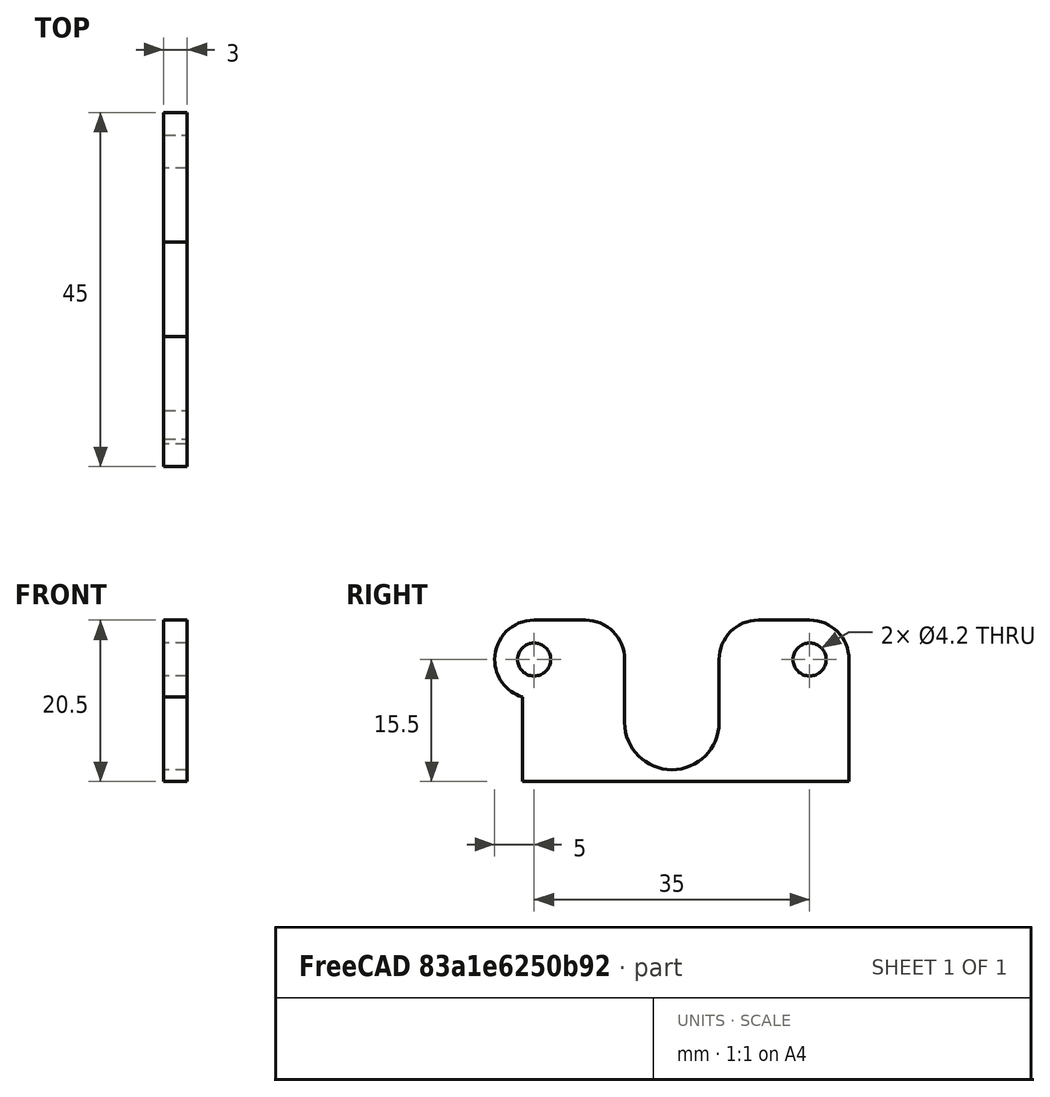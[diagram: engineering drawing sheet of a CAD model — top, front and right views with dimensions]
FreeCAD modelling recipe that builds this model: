
FCSTD DOCUMENT  (FreeCAD 0.16R6712 (Git))
Label: stepperMount_v01
License: All rights reserved
LicenseURL: http://en.wikipedia.org/wiki/All_rights_reserved
objects: Sketcher::SketchObject×1, PartDesign::Pad×1
note: 3 computed .brp shape members not serialized (recipe doc carries the construction recipe); baked Part::Feature solids carry a one-line shape summary decoded from their .brp

FEATURE [Sketcher::SketchObject] Sketch  label="StepperMount"
  Placement = pos=(0,0,0) rot=(0.57735,0.57735,0.57735;2.0944rad)
  sketch-geometry (15):
    g0: Circle CenterX=-17.5 CenterY=14 CenterZ=0 NormalX=0 NormalY=0 NormalZ=1 Radius=2.1
    g1: Circle CenterX=17.5 CenterY=14 CenterZ=0 NormalX=0 NormalY=0 NormalZ=1 Radius=2.1
    g2: ArcOfCircle CenterX=-17.5 CenterY=14 CenterZ=0 NormalX=0 NormalY=0 NormalZ=1 Radius=5 StartAngle=1.5708 EndAngle=3.14159
    g3: ArcOfCircle CenterX=17.5 CenterY=14 CenterZ=0 NormalX=0 NormalY=0 NormalZ=1 Radius=5 StartAngle=0 EndAngle=1.5708
    g4: ArcOfCircle CenterX=0 CenterY=6 CenterZ=0 NormalX=0 NormalY=0 NormalZ=1 Radius=6 StartAngle=3.14159 EndAngle=6.28319
    g5: LineSegment StartX=-6 StartY=6 StartZ=0 EndX=-6 EndY=14 EndZ=0
    g6: LineSegment StartX=6 StartY=6 StartZ=0 EndX=6 EndY=14 EndZ=0
    g7: ArcOfCircle CenterX=-11 CenterY=14 CenterZ=0 NormalX=0 NormalY=0 NormalZ=1 Radius=5 StartAngle=0 EndAngle=1.5708
    g8: ArcOfCircle CenterX=11 CenterY=14 CenterZ=0 NormalX=0 NormalY=0 NormalZ=1 Radius=5 StartAngle=1.5708 EndAngle=3.14159
    g9: LineSegment StartX=-17.5 StartY=19 StartZ=0 EndX=-11 EndY=19 EndZ=0
    g10: LineSegment StartX=11 StartY=19 StartZ=0 EndX=17.5 EndY=19 EndZ=0
    g11: ArcOfCircle CenterX=-17.5 CenterY=14 CenterZ=0 NormalX=0 NormalY=0 NormalZ=1 Radius=5 StartAngle=3.14159 EndAngle=4.4077
    g12: LineSegment StartX=-19 StartY=9.2303 StartZ=0 EndX=-19 EndY=-1.5 EndZ=0
    g13: LineSegment StartX=22.5 StartY=14 StartZ=0 EndX=22.5 EndY=-1.5 EndZ=0
    g14: LineSegment StartX=-19 StartY=-1.5 StartZ=0 EndX=22.5 EndY=-1.5 EndZ=0
  constraints (47):
    c: Radius(g0) = 2.1
    c: Equal(g0,g1)
    c: DistanceX(g0,g1) = 35
    c: Symmetric(g0,g1,g-2)
    c: Coincident(g2,g0)
    c: DistanceX(g2,g0) = 5
    c: DistanceX(g0,g2) = 0
    c: Coincident(g3,g1)
    c: DistanceX(g1,g3) = 5
    c: DistanceX(g3,g1) = 0
    c: DistanceY(g-1,g4) = 6
    c: DistanceY(g4,g2) = 8
    c: DistanceY(g4,g3) = 8
    c: DistanceY(g-1,g4) = 6
    c: DistanceX(g4,g4) = 6
    c: DistanceX(g-1,g4) = 0
    c: DistanceY(g-1,g4) = 6
    c: Coincident(g5,g4)
    c: Vertical(g5)
    c: DistanceY(g4,g5) = 8
    c: Coincident(g6,g4)
    c: Vertical(g6)
    c: DistanceY(g4,g6) = 8
    c: Coincident(g7,g5)
    c: DistanceX(g7,g5) = 5
    c: DistanceY(g4,g7) = 8
    c: DistanceX(g7,g5) = 5
    c: Coincident(g8,g6)
    c: DistanceX(g6,g8) = 5
    c: DistanceY(g4,g8) = 8
    c: DistanceX(g8,g8) = 0
    c: Coincident(g9,g2)
    c: Coincident(g9,g7)
    c: Horizontal(g9)
    c: Coincident(g10,g8)
    c: Coincident(g10,g3)
    c: DistanceY(g13,g-1) = 1.5
    c: Coincident(g11,g0)
    c: Coincident(g11,g2)
    c: Coincident(g12,g11)
    c: Vertical(g12)
    c: DistanceX(g12,g-1) = 19
    c: Coincident(g13,g3)
    c: Vertical(g13)
    c: Coincident(g14,g12)
    c: Coincident(g14,g13)
    c: Horizontal(g14)
FEATURE [PartDesign::Pad] Pad
  Length = 3
  Length2 = 100
  Placement = pos=(0,0,0) rot=(0.57735,0.57735,0.57735;2.0944rad)
  Sketch = -> Sketch
  Type = 0
